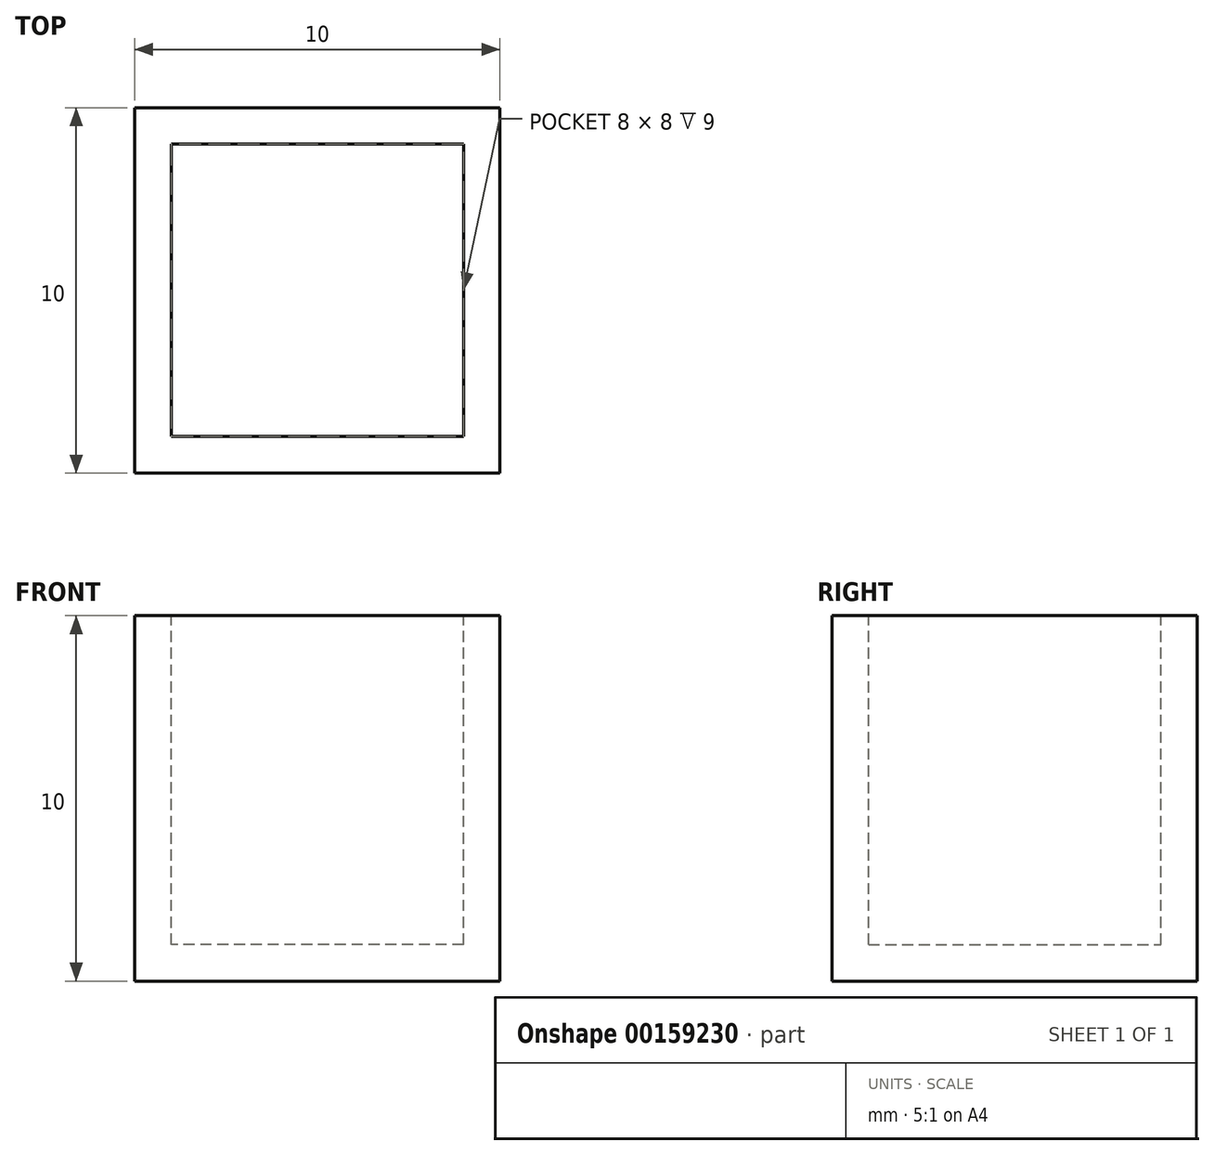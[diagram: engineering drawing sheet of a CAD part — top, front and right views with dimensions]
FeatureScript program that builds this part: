
annotation { "Feature Type Name" : "Feature", "Feature Type Description" : "" }
export const myFeature = defineFeature(function(context is Context, id is Id, definition is map)
    precondition{}
    {
        {
            var Q0;
            Q0=qCreatedBy(makeId("Top.planeOp"),FACE);
            var sketch = newSketch(context, id + "F0", { "sketchPlane" : qUnion([Q0])});
            skLineSegment(sketch, "E0.bottom", {"start": v(-5, 5) * mm, "end": v(5, 5) * mm});
            skLineSegment(sketch, "E0.top", {"start": v(-5, -5) * mm, "end": v(5, -5) * mm});
            skLineSegment(sketch, "E0.left", {"start": v(-5, 5) * mm, "end": v(-5, -5) * mm});
            skLineSegment(sketch, "E0.right", {"start": v(5, 5) * mm, "end": v(5, -5) * mm});
            skPoint(sketch, "E1", {"position": v(0, 0) * mm});
            skPoint(sketch, "E1.positionSnap0", {"position": v(-5, 0) * mm});
            skPoint(sketch, "E1.positionSnap1", {"position": v(0, 5) * mm});
            skSolve(sketch);
        }
        {
            var Q0;
            Q0=qSketchRegion(id+"F0",true);
            extrude(context, id + "F1", {"entities" : qUnion([Q0]), "depth" : 10 * mm});
        }
        {
            var Q0;
            Q0=makeQuery(id+"F1.opExtrude","CAP_FACE",FACE,{"disambiguationData":[OSD([sQuery(id+"F0.wireOp",EDGE,"E0.bottom"),sQuery(id+"F0.wireOp",EDGE,"E0.top"),sQuery(id+"F0.wireOp",EDGE,"E0.left"),sQuery(id+"F0.wireOp",EDGE,"E0.right")])],"isStart":false});
            var sketch = newSketch(context, id + "F2", { "sketchPlane" : qUnion([Q0])});
            skLineSegment(sketch, "E2.bottom", {"start": v(4, -4) * mm, "end": v(-4, -4) * mm});
            skLineSegment(sketch, "E2.top", {"start": v(4, 4) * mm, "end": v(-4, 4) * mm});
            skLineSegment(sketch, "E2.left", {"start": v(4, -4) * mm, "end": v(4, 4) * mm});
            skLineSegment(sketch, "E2.right", {"start": v(-4, -4) * mm, "end": v(-4, 4) * mm});
            skPoint(sketch, "E2.middle", {"position": v(0, 0) * mm});
            skSolve(sketch);
        }
        {
            var Q0;
            Q0=makeQuery(id+"F2.imprint","IMPRINT",FACE,{"disambiguationData":[TD([[makeQuery(id+"F2.imprint","IMPRINT",EDGE,{"derivedFrom":sQuery(id+"F2.wireOp",EDGE,"E2.bottom")}),-1.0]])]});
            extrude(context, id + "F3", {"entities" : qUnion([Q0]), "operationType" : NewBodyOperationType.REMOVE, "oppositeDirection" : true, "depth" : 9 * mm});
        }
    });
